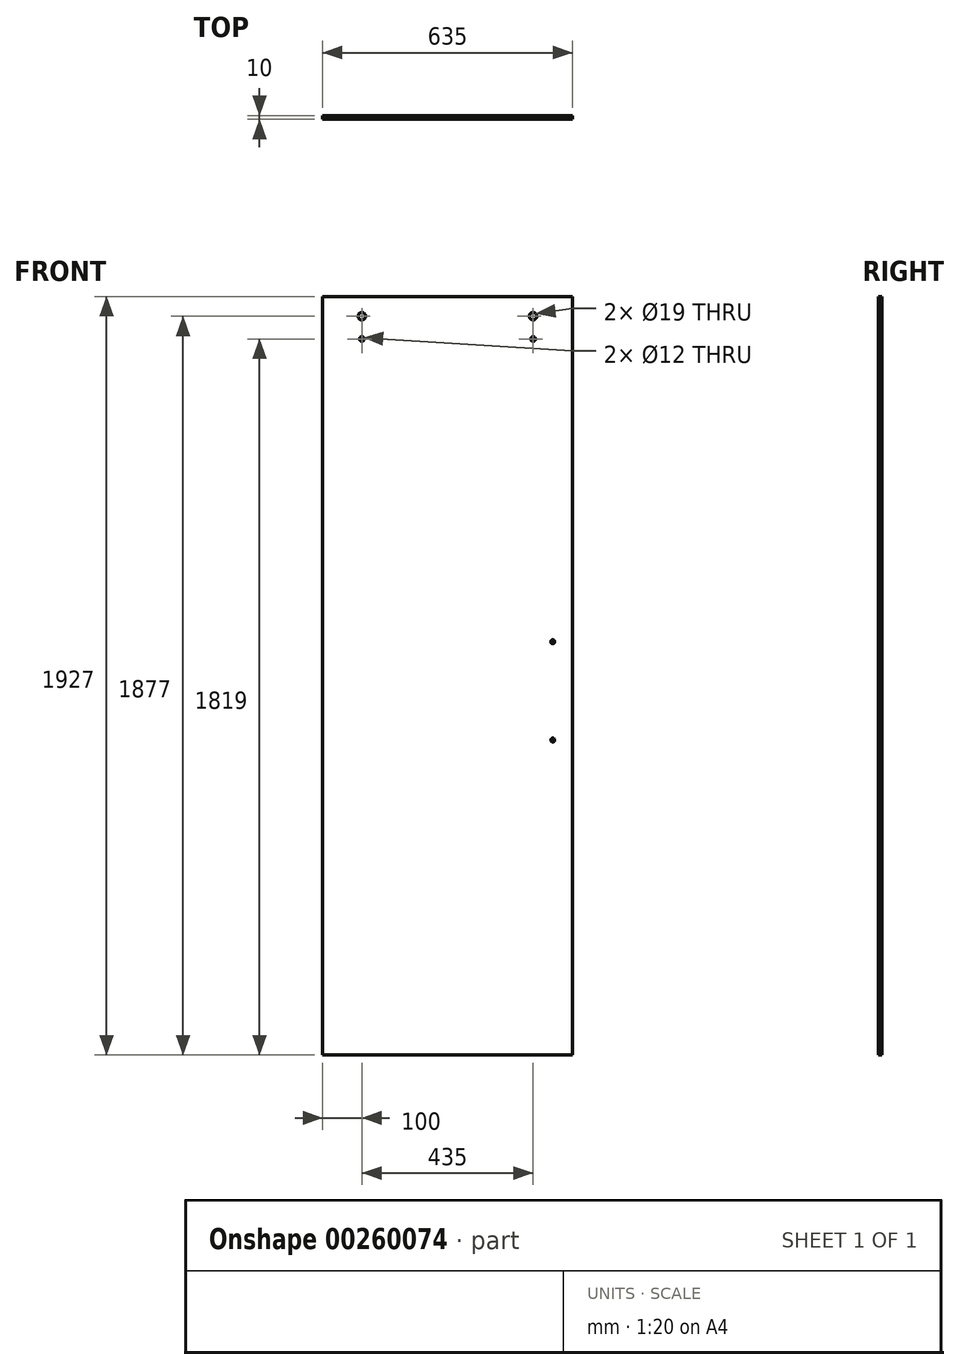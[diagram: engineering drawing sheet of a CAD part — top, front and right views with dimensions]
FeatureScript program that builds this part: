
annotation { "Feature Type Name" : "Feature", "Feature Type Description" : "" }
export const myFeature = defineFeature(function(context is Context, id is Id, definition is map)
    precondition{}
    {
        {
            var Q0;
            Q0=qCreatedBy(makeId("Front.planeOp"),FACE);
            var sketch = newSketch(context, id + "F0", { "sketchPlane" : qUnion([Q0]), "disableImprinting" : false});
            skLineSegment(sketch, "E0.bottom", {"start": v(317.5, -963.5) * mm, "end": v(-317.5, -963.5) * mm});
            skLineSegment(sketch, "E0.top", {"start": v(317.5, 963.5) * mm, "end": v(-317.5, 963.5) * mm});
            skLineSegment(sketch, "E0.left", {"start": v(317.5, -963.5) * mm, "end": v(317.5, 963.5) * mm});
            skLineSegment(sketch, "E0.right", {"start": v(-317.5, -963.5) * mm, "end": v(-317.5, 963.5) * mm});
            skPoint(sketch, "E0.middle", {"position": v(0, 0) * mm});
            skLineSegment(sketch, "E1", {"start": v(-401.03, 913.5) * mm, "end": v(480.45, 913.5) * mm, "construction": true});
            skLineSegment(sketch, "E2", {"start": v(-406.43, 855.5) * mm, "end": v(466.4, 855.5) * mm, "construction": true});
            skLineSegment(sketch, "E3", {"start": v(217.5, 999.67) * mm, "end": v(217.5, 619.43) * mm, "construction": true});
            skLineSegment(sketch, "E4", {"start": v(-217.5, 991.03) * mm, "end": v(-217.5, 609.06) * mm, "construction": true});
            skCircle(sketch, "E5", {"center": v(-217.5, 913.5) * mm, "radius": 9.5 * mm});
            skCircle(sketch, "E6", {"center": v(-217.5, 855.5) * mm, "radius": 6 * mm});
            skCircle(sketch, "E7", {"center": v(217.5, 855.5) * mm, "radius": 6 * mm});
            skCircle(sketch, "E8", {"center": v(217.5, 913.5) * mm, "radius": 9.5 * mm});
            skLineSegment(sketch, "E9", {"start": v(267.5, 86.5) * mm, "end": v(267.5, -163.5) * mm, "construction": true});
            skCircle(sketch, "E10", {"center": v(267.5, 86.5) * mm, "radius": 5 * mm});
            skCircle(sketch, "E11", {"center": v(267.5, -163.5) * mm, "radius": 5 * mm});
            skSolve(sketch);
        }
        {
            var Q0;
            Q0=makeQuery(id+"F0.imprint","IMPRINT",FACE,{"disambiguationData":[TD([[makeQuery(id+"F0.imprint","IMPRINT",EDGE,{"derivedFrom":sQuery(id+"F0.wireOp",EDGE,"E0.bottom")}),-1.0]])]});
            extrude(context, id + "F1", {"entities" : qUnion([Q0]), "depth" : 10 * mm});
        }
    });
